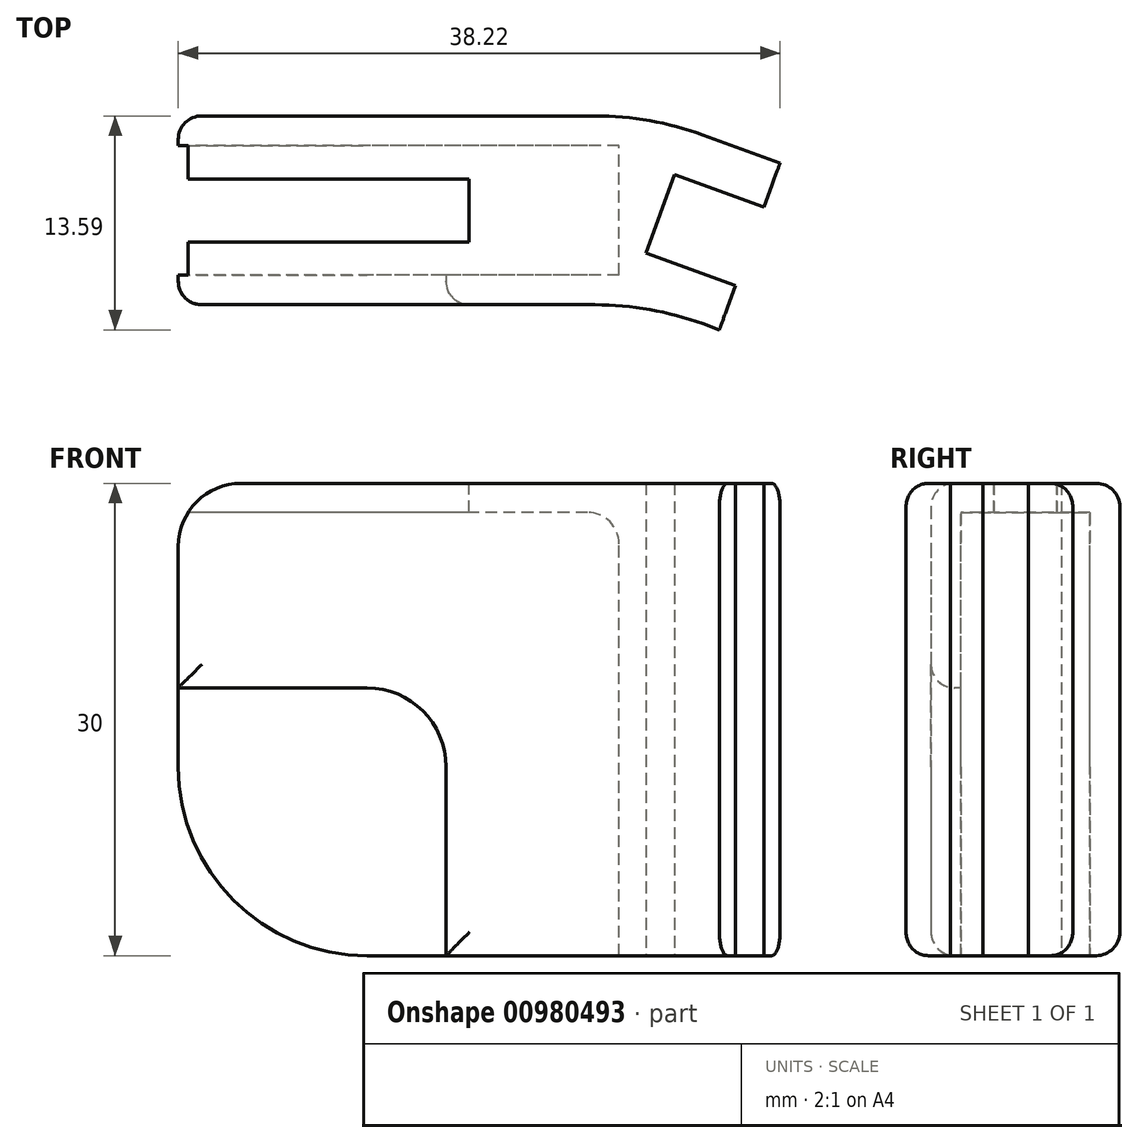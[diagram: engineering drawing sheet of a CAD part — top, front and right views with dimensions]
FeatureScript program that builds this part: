
annotation { "Feature Type Name" : "Feature", "Feature Type Description" : "" }
export const myFeature = defineFeature(function(context is Context, id is Id, definition is map)
    precondition{}
    {
        {
            var Q0;
            Q0=qCreatedBy(makeId("Top.planeOp"),FACE);
            var sketch = newSketch(context, id + "F0", { "sketchPlane" : qUnion([Q0])});
            skLineSegment(sketch, "E0.bottom", {"start": v(0, 0) * mm, "end": v(-30, 0) * mm});
            skLineSegment(sketch, "E0.top", {"start": v(0, 12) * mm, "end": v(-30, 12) * mm});
            skLineSegment(sketch, "E0.left", {"start": v(0, 0) * mm, "end": v(0, 12) * mm});
            skLineSegment(sketch, "E0.right", {"start": v(-30, 0) * mm, "end": v(-30, 12) * mm});
            skLineSegment(sketch, "E1", {"start": v(0, 12) * mm, "end": v(7.52, 9.26) * mm});
            skLineSegment(sketch, "E2", {"start": v(7.52, 9.26) * mm, "end": v(3.66, -1.33) * mm});
            skLineSegment(sketch, "E3", {"start": v(3.66, -1.33) * mm, "end": v(0, 0) * mm});
            skSolve(sketch);
        }
        {
            var Q0;
            Q0=makeQuery(id+"F0.imprint","IMPRINT",FACE,{"disambiguationData":[TD([[makeQuery(id+"F0.imprint","IMPRINT",EDGE,{"derivedFrom":sQuery(id+"F0.wireOp",EDGE,"E0.bottom")}),-1.0]])]});
            var Q1;
            Q1=makeQuery(id+"F0.imprint","IMPRINT",FACE,{"disambiguationData":[TD([[makeQuery(id+"F0.imprint","IMPRINT",EDGE,{"derivedFrom":sQuery(id+"F0.wireOp",EDGE,"E0.left")}),-1.0]])]});
            extrude(context, id + "F1", {"entities" : qUnion([Q0, Q1]), "depth" : 30 * mm, "offsetDistance" : 25 * mm});
        }
        {
            var Q0;
            Q0=makeQuery(id+"F1.opExtrude","SWEPT_FACE",FACE,{"disambiguationData":[OSD([sQuery(id+"F0.wireOp",EDGE,"E0.right")])]});
            var sketch = newSketch(context, id + "F2", { "sketchPlane" : qUnion([Q0])});
            skLineSegment(sketch, "E4.bottom", {"start": v(-10.1, 0) * mm, "end": v(-1.9, 0) * mm});
            skLineSegment(sketch, "E4.top", {"start": v(-10.1, 28.15) * mm, "end": v(-1.9, 28.15) * mm});
            skLineSegment(sketch, "E4.left", {"start": v(-10.1, 0) * mm, "end": v(-10.1, 28.15) * mm});
            skLineSegment(sketch, "E4.right", {"start": v(-1.9, 0) * mm, "end": v(-1.9, 28.15) * mm});
            skLineSegment(sketch, "E5", {"start": v(-10.1, 20.28) * mm, "end": v(-12, 20.28) * mm, "construction": true});
            skLineSegment(sketch, "E6", {"start": v(-1.9, 13.43) * mm, "end": v(0, 13.43) * mm, "construction": true});
            skSolve(sketch);
        }
        {
            var Q0;
            Q0=makeQuery(id+"F2.imprint","IMPRINT",FACE,{"disambiguationData":[TD([[makeQuery(id+"F2.imprint","IMPRINT",EDGE,{"derivedFrom":sQuery(id+"F2.wireOp",EDGE,"E4.bottom")}),-1.0]])]});
            extrude(context, id + "F3", {"entities" : qUnion([Q0]), "operationType" : NewBodyOperationType.REMOVE, "oppositeDirection" : true, "depth" : 28 * mm, "offsetDistance" : 25 * mm});
        }
        {
            var Q0;
            Q0=makeQuery(id+"F1.opExtrude","SWEPT_FACE",FACE,{"disambiguationData":[OSD([sQuery(id+"F0.wireOp",EDGE,"E2")])]});
            var sketch = newSketch(context, id + "F4", { "sketchPlane" : qUnion([Q0])});
            skLineSegment(sketch, "E7", {"start": v(2.99, 30) * mm, "end": v(2.99, 0) * mm});
            skLineSegment(sketch, "E8", {"start": v(8.29, 30) * mm, "end": v(8.29, 0) * mm});
            skLineSegment(sketch, "E9", {"start": v(0, 29.88) * mm, "end": v(2.99, 29.88) * mm, "construction": true});
            skLineSegment(sketch, "E10", {"start": v(8.29, 6.77) * mm, "end": v(11.28, 6.77) * mm, "construction": true});
            skSolve(sketch);
        }
        {
            var Q0;
            {var subQ0=sQuery(id+"F4.wireOp",EDGE,"E7");Q0=makeQuery(id+"F4.imprint","IMPRINT",FACE,{"disambiguationData":[TD([[makeQuery(id+"F4.imprint","IMPRINT",EDGE,{"derivedFrom":subQ0}),1.0]])]});}
            extrude(context, id + "F5", {"entities" : qUnion([Q0]), "operationType" : NewBodyOperationType.REMOVE, "oppositeDirection" : true, "depth" : 5.3 * mm, "offsetDistance" : 25 * mm});
        }
        {
            var Q0;
            Q0=makeQuery(id+"F1.opExtrude","SWEPT_FACE",FACE,{"disambiguationData":[OSD([sQuery(id+"F0.wireOp",EDGE,"E0.bottom")])]});
            var sketch = newSketch(context, id + "F6", { "sketchPlane" : qUnion([Q0])});
            skLineSegment(sketch, "E11.bottom", {"start": v(-30, 17) * mm, "end": v(-13, 17) * mm});
            skLineSegment(sketch, "E11.top", {"start": v(-30, 0) * mm, "end": v(-13, 0) * mm});
            skLineSegment(sketch, "E11.left", {"start": v(-30, 17) * mm, "end": v(-30, 0) * mm});
            skLineSegment(sketch, "E11.right", {"start": v(-13, 17) * mm, "end": v(-13, 0) * mm});
            skSolve(sketch);
        }
        {
            var Q0;
            Q0=makeQuery(id+"F6.imprint","IMPRINT",FACE,{"disambiguationData":[TD([[makeQuery(id+"F6.imprint","IMPRINT",EDGE,{"derivedFrom":sQuery(id+"F6.wireOp",EDGE,"E11.bottom")}),-1.0]])]});
            extrude(context, id + "F7", {"entities" : qUnion([Q0]), "operationType" : NewBodyOperationType.REMOVE, "oppositeDirection" : true, "depth" : 2.8 * mm, "offsetDistance" : 25 * mm});
        }
        {
            var Q0;
            {var subQ1=sQuery(id+"F0.wireOp",EDGE,"E2");var subQ2=sQuery(id+"F0.wireOp",EDGE,"E1");Q0=makeQuery(id+"F5.boolean.opBoolean","SPLIT",FACE,{"disambiguationData":[TD([makeQuery(id+"F1.opExtrude","SWEPT_FACE",FACE,{"disambiguationData":[OSD([subQ2])]})])],"derivedFrom":makeQuery(id+"F1.opExtrude","SWEPT_FACE",FACE,{"disambiguationData":[OSD([subQ1])]})});}
            var Q1;
            {var subQ0=sQuery(id+"F0.wireOp",EDGE,"E3");var subQ1=sQuery(id+"F0.wireOp",EDGE,"E2");Q1=makeQuery(id+"F5.boolean.opBoolean","SPLIT",FACE,{"disambiguationData":[TD([makeQuery(id+"F1.opExtrude","SWEPT_FACE",FACE,{"disambiguationData":[OSD([subQ0])]})])],"derivedFrom":makeQuery(id+"F1.opExtrude","SWEPT_FACE",FACE,{"disambiguationData":[OSD([subQ1])]})});}
            extrude(context, id + "F8", {"entities" : qUnion([Q0, Q1]), "operationType" : NewBodyOperationType.ADD, "depth" : .75 * mm, "offsetDistance" : 25 * mm});
        }
        {
            var Q0;
            {var subQ0=sQuery(id+"F0.wireOp",EDGE,"E0.right");var subQ1=sQuery(id+"F0.wireOp",EDGE,"E0.top");Q0=makeQuery(id+"F3.boolean.opBoolean","SPLIT",EDGE,{"disambiguationData":[TD([makeQuery(id+"F1.opExtrude","SWEPT_FACE",FACE,{"disambiguationData":[OSD([subQ1])]})])],"derivedFrom":makeQuery(id+"F1.opExtrude","CAP_EDGE",EDGE,{"disambiguationData":[OSD([subQ0])],"isStart":true})});}
            fillet(context, id + "F9", {"entities" : qUnion([Q0]), "radius" : 12 * mm, "tangentPropagation" : true, "allowEdgeOverflow" : false});
        }
        {
            var Q0;
            Q0=makeQuery(id+"F1.opExtrude","CAP_EDGE",EDGE,{"disambiguationData":[OSD([sQuery(id+"F0.wireOp",EDGE,"E0.right")])],"isStart":false});
            var Q1;
            Q1=makeQuery(id+"F7.boolean.opBoolean","COPY",EDGE,{"derivedFrom":makeQuery(id+"F7.opExtrude","SWEPT_EDGE",EDGE,{"disambiguationData":[OSD([sQuery(id+"F0.wireOp",EDGE,"E0.bottom"),sQuery(id+"F0.wireOp",EDGE,"E0.right"),sQuery(id+"F6.wireOp",EDGE,"E11.bottom"),sQuery(id+"F6.wireOp",EDGE,"E11.left")])]})});
            var Q2;
            Q2=makeQuery(id+"F7.boolean.opBoolean","COPY",EDGE,{"derivedFrom":makeQuery(id+"F7.opExtrude","SWEPT_EDGE",EDGE,{"disambiguationData":[OSD([sQuery(id+"F0.wireOp",EDGE,"E0.bottom"),sQuery(id+"F6.wireOp",EDGE,"E11.top"),sQuery(id+"F6.wireOp",EDGE,"E11.right")])]})});
            fillet(context, id + "F10", {"entities" : qUnion([Q0, Q1, Q2]), "radius" : 4 * mm, "tangentPropagation" : true, "allowEdgeOverflow" : false});
        }
        {
            var Q0;
            Q0=makeQuery(id+"F1.opExtrude","SWEPT_EDGE",EDGE,{"disambiguationData":[OSD([sQuery(id+"F0.wireOp",EDGE,"E0.top"),sQuery(id+"F0.wireOp",EDGE,"E0.left"),sQuery(id+"F0.wireOp",EDGE,"E1")])]});
            var Q1;
            Q1=makeQuery(id+"F1.opExtrude","SWEPT_EDGE",EDGE,{"disambiguationData":[OSD([sQuery(id+"F0.wireOp",EDGE,"E0.bottom"),sQuery(id+"F0.wireOp",EDGE,"E0.left"),sQuery(id+"F0.wireOp",EDGE,"E3")])]});
            fillet(context, id + "F11", {"entities" : qUnion([Q0, Q1]), "radius" : 20 * mm, "tangentPropagation" : true, "allowEdgeOverflow" : false});
        }
        {
            var Q0;
            Q0=makeQuery(id+"F7.boolean.opBoolean","COPY",EDGE,{"derivedFrom":makeQuery(id+"F7.opExtrude","SWEPT_EDGE",EDGE,{"disambiguationData":[OSD([sQuery(id+"F6.wireOp",EDGE,"E11.bottom"),sQuery(id+"F6.wireOp",EDGE,"E11.right")])]})});
            fillet(context, id + "F12", {"entities" : qUnion([Q0]), "radius" : 5 * mm, "tangentPropagation" : true, "allowEdgeOverflow" : false});
        }
        {
            var Q0;
            Q0=makeQuery(id+"F12.opFillet","BLEND_EDGE",EDGE,{"blendedFrom":[makeQuery(id+"F7.boolean.opBoolean","COPY",EDGE,{"derivedFrom":makeQuery(id+"F7.opExtrude","SWEPT_EDGE",EDGE,{"disambiguationData":[OSD([sQuery(id+"F6.wireOp",EDGE,"E11.bottom"),sQuery(id+"F6.wireOp",EDGE,"E11.right")])]})}),makeQuery(id+"F1.opExtrude","SWEPT_FACE",FACE,{"disambiguationData":[OSD([sQuery(id+"F0.wireOp",EDGE,"E0.bottom")])]})],"blendedInto":[makeQuery(id+"F1.opExtrude","SWEPT_FACE",FACE,{"disambiguationData":[OSD([sQuery(id+"F0.wireOp",EDGE,"E0.bottom")])]})]});
            var Q1;
            Q1=makeQuery(id+"F7.boolean.opBoolean","COPY",EDGE,{"derivedFrom":makeQuery(id+"F7.opExtrude","CAP_EDGE",EDGE,{"disambiguationData":[OSD([sQuery(id+"F6.wireOp",EDGE,"E11.bottom")])],"isStart":true})});
            var Q2;
            Q2=makeQuery(id+"F10.opFillet","BLEND_EDGE",EDGE,{"blendedFrom":[makeQuery(id+"F1.opExtrude","CAP_EDGE",EDGE,{"disambiguationData":[OSD([sQuery(id+"F0.wireOp",EDGE,"E0.right")])],"isStart":false}),makeQuery(id+"F1.opExtrude","SWEPT_FACE",FACE,{"disambiguationData":[OSD([sQuery(id+"F0.wireOp",EDGE,"E0.bottom")])]})],"blendedInto":[makeQuery(id+"F1.opExtrude","SWEPT_FACE",FACE,{"disambiguationData":[OSD([sQuery(id+"F0.wireOp",EDGE,"E0.bottom")])]})]});
            var Q3;
            Q3=makeQuery(id+"F1.opExtrude","CAP_EDGE",EDGE,{"disambiguationData":[OSD([sQuery(id+"F0.wireOp",EDGE,"E0.bottom")])],"isStart":false});
            var Q4;
            {var subQ0=sQuery(id+"F0.wireOp",EDGE,"E3");var subQ1=sQuery(id+"F0.wireOp",EDGE,"E0.bottom");Q4=makeQuery(id+"F11.opFillet","BLEND_EDGE",EDGE,{"blendedFrom":[makeQuery(id+"F1.opExtrude","SWEPT_EDGE",EDGE,{"disambiguationData":[OSD([subQ1,sQuery(id+"F0.wireOp",EDGE,"E0.left"),subQ0])]}),makeQuery(id+"F1.opExtrude","CAP_FACE",FACE,{"disambiguationData":[OSD([subQ1,sQuery(id+"F0.wireOp",EDGE,"E0.top"),sQuery(id+"F0.wireOp",EDGE,"E0.right"),sQuery(id+"F0.wireOp",EDGE,"E1"),sQuery(id+"F0.wireOp",EDGE,"E2"),subQ0])],"isStart":false})],"blendedInto":[makeQuery(id+"F1.opExtrude","CAP_FACE",FACE,{"disambiguationData":[OSD([subQ1,sQuery(id+"F0.wireOp",EDGE,"E0.top"),sQuery(id+"F0.wireOp",EDGE,"E0.right"),sQuery(id+"F0.wireOp",EDGE,"E1"),sQuery(id+"F0.wireOp",EDGE,"E2"),subQ0])],"isStart":false})]});}
            var Q5;
            Q5=makeQuery(id+"F1.opExtrude","CAP_EDGE",EDGE,{"disambiguationData":[OSD([sQuery(id+"F0.wireOp",EDGE,"E3")])],"isStart":false});
            var Q6;
            Q6=makeQuery(id+"F1.opExtrude","SWEPT_EDGE",EDGE,{"disambiguationData":[OSD([sQuery(id+"F0.wireOp",EDGE,"E2"),sQuery(id+"F0.wireOp",EDGE,"E3")])]});
            var Q7;
            Q7=makeQuery(id+"F1.opExtrude","CAP_EDGE",EDGE,{"disambiguationData":[OSD([sQuery(id+"F0.wireOp",EDGE,"E3")])],"isStart":true});
            var Q8;
            {var subQ0=sQuery(id+"F0.wireOp",EDGE,"E3");var subQ1=sQuery(id+"F0.wireOp",EDGE,"E0.bottom");Q8=makeQuery(id+"F11.opFillet","BLEND_EDGE",EDGE,{"blendedFrom":[makeQuery(id+"F1.opExtrude","SWEPT_EDGE",EDGE,{"disambiguationData":[OSD([subQ1,sQuery(id+"F0.wireOp",EDGE,"E0.left"),subQ0])]}),makeQuery(id+"F1.opExtrude","CAP_FACE",FACE,{"disambiguationData":[OSD([subQ1,sQuery(id+"F0.wireOp",EDGE,"E0.top"),sQuery(id+"F0.wireOp",EDGE,"E0.right"),sQuery(id+"F0.wireOp",EDGE,"E1"),sQuery(id+"F0.wireOp",EDGE,"E2"),subQ0])],"isStart":true})],"blendedInto":[makeQuery(id+"F1.opExtrude","CAP_FACE",FACE,{"disambiguationData":[OSD([subQ1,sQuery(id+"F0.wireOp",EDGE,"E0.top"),sQuery(id+"F0.wireOp",EDGE,"E0.right"),sQuery(id+"F0.wireOp",EDGE,"E1"),sQuery(id+"F0.wireOp",EDGE,"E2"),subQ0])],"isStart":true})]});}
            var Q9;
            Q9=makeQuery(id+"F1.opExtrude","CAP_EDGE",EDGE,{"disambiguationData":[OSD([sQuery(id+"F0.wireOp",EDGE,"E0.bottom")])],"isStart":true});
            var Q10;
            {var subQ0=sQuery(id+"F0.wireOp",EDGE,"E0.bottom");Q10=makeQuery(id+"F10.opFillet","BLEND_EDGE",EDGE,{"blendedFrom":[makeQuery(id+"F7.boolean.opBoolean","COPY",EDGE,{"derivedFrom":makeQuery(id+"F7.opExtrude","SWEPT_EDGE",EDGE,{"disambiguationData":[OSD([subQ0,sQuery(id+"F6.wireOp",EDGE,"E11.top"),sQuery(id+"F6.wireOp",EDGE,"E11.right")])]})}),makeQuery(id+"F1.opExtrude","SWEPT_FACE",FACE,{"disambiguationData":[OSD([subQ0])]})],"blendedInto":[makeQuery(id+"F1.opExtrude","SWEPT_FACE",FACE,{"disambiguationData":[OSD([subQ0])]})]});}
            var Q11;
            Q11=makeQuery(id+"F7.boolean.opBoolean","COPY",EDGE,{"derivedFrom":makeQuery(id+"F7.opExtrude","CAP_EDGE",EDGE,{"disambiguationData":[OSD([sQuery(id+"F6.wireOp",EDGE,"E11.right")])],"isStart":true})});
            var Q12;
            Q12=makeQuery(id+"F1.opExtrude","CAP_EDGE",EDGE,{"disambiguationData":[OSD([sQuery(id+"F0.wireOp",EDGE,"E0.top")])],"isStart":false});
            var Q13;
            {var subQ0=sQuery(id+"F0.wireOp",EDGE,"E1");var subQ1=sQuery(id+"F0.wireOp",EDGE,"E0.top");Q13=makeQuery(id+"F11.opFillet","BLEND_EDGE",EDGE,{"blendedFrom":[makeQuery(id+"F1.opExtrude","SWEPT_EDGE",EDGE,{"disambiguationData":[OSD([subQ1,sQuery(id+"F0.wireOp",EDGE,"E0.left"),subQ0])]}),makeQuery(id+"F1.opExtrude","CAP_FACE",FACE,{"disambiguationData":[OSD([sQuery(id+"F0.wireOp",EDGE,"E0.bottom"),subQ1,sQuery(id+"F0.wireOp",EDGE,"E0.right"),subQ0,sQuery(id+"F0.wireOp",EDGE,"E2"),sQuery(id+"F0.wireOp",EDGE,"E3")])],"isStart":false})],"blendedInto":[makeQuery(id+"F1.opExtrude","CAP_FACE",FACE,{"disambiguationData":[OSD([sQuery(id+"F0.wireOp",EDGE,"E0.bottom"),subQ1,sQuery(id+"F0.wireOp",EDGE,"E0.right"),subQ0,sQuery(id+"F0.wireOp",EDGE,"E2"),sQuery(id+"F0.wireOp",EDGE,"E3")])],"isStart":false})]});}
            var Q14;
            Q14=makeQuery(id+"F1.opExtrude","SWEPT_EDGE",EDGE,{"disambiguationData":[OSD([sQuery(id+"F0.wireOp",EDGE,"E1"),sQuery(id+"F0.wireOp",EDGE,"E2")])]});
            fillet(context, id + "F13", {"entities" : qUnion([Q0, Q1, Q2, Q3, Q4, Q5, Q6, Q7, Q8, Q9, Q10, Q11, Q12, Q13, Q14]), "radius" : 1.5 * mm, "tangentPropagation" : true, "allowEdgeOverflow" : false});
        }
        {
            var Q0;
            Q0=makeQuery(id+"F3.boolean.opBoolean","COPY",EDGE,{"derivedFrom":makeQuery(id+"F3.opExtrude","CAP_EDGE",EDGE,{"disambiguationData":[OSD([sQuery(id+"F2.wireOp",EDGE,"E4.top")])],"isStart":false})});
            fillet(context, id + "F14", {"entities" : qUnion([Q0]), "radius" : 2 * mm, "tangentPropagation" : true, "allowEdgeOverflow" : false});
        }
        {
            var Q0;
            {var subQ0=sQuery(id+"F0.wireOp",EDGE,"E3");var subQ1=sQuery(id+"F0.wireOp",EDGE,"E2");var subQ2=sQuery(id+"F0.wireOp",EDGE,"E1");var subQ3=makeQuery(id+"F1.opExtrude","CAP_FACE",FACE,{"disambiguationData":[OSD([sQuery(id+"F0.wireOp",EDGE,"E0.bottom"),sQuery(id+"F0.wireOp",EDGE,"E0.top"),sQuery(id+"F0.wireOp",EDGE,"E0.right"),subQ2,subQ1,subQ0])],"isStart":false});var subQ5=makeQuery(id+"F1.opExtrude","CAP_EDGE",EDGE,{"disambiguationData":[OSD([subQ1])],"isStart":false});Q0=makeQuery(id+"F8.boolean.opBoolean","MERGE",FACE,{"derivedFrom":[subQ3,makeQuery(id+"F8.opExtrude","SWEPT_FACE",FACE,{"disambiguationData":[OSD([subQ1]),TDD([makeQuery(id+"F5.boolean.opBoolean","SPLIT",EDGE,{"disambiguationData":[TD([makeQuery(id+"F1.opExtrude","SWEPT_FACE",FACE,{"disambiguationData":[OSD([subQ2])]})])],"derivedFrom":subQ5})])]}),makeQuery(id+"F8.opExtrude","SWEPT_FACE",FACE,{"disambiguationData":[OSD([subQ1]),TDD([makeQuery(id+"F5.boolean.opBoolean","SPLIT",EDGE,{"disambiguationData":[TD([makeQuery(id+"F1.opExtrude","SWEPT_FACE",FACE,{"disambiguationData":[OSD([subQ0])]})])],"derivedFrom":subQ5})])]})]});}
            var sketch = newSketch(context, id + "F15", { "sketchPlane" : qUnion([Q0])});
            skLineSegment(sketch, "E12", {"start": v(-31.09, 6) * mm, "end": v(6.32, 6) * mm, "construction": true});
            skPoint(sketch, "E12.startSnap0", {"position": v(-26, 6) * mm});
            skLineSegment(sketch, "E13.bottom", {"start": v(-31.09, 8) * mm, "end": v(-11.53, 8) * mm});
            skLineSegment(sketch, "E13.top", {"start": v(-31.09, 4) * mm, "end": v(-11.53, 4) * mm});
            skLineSegment(sketch, "E13.left", {"start": v(-31.09, 8) * mm, "end": v(-31.09, 4) * mm});
            skLineSegment(sketch, "E13.right", {"start": v(-11.53, 8) * mm, "end": v(-11.53, 4) * mm});
            skSolve(sketch);
        }
        {
            var Q0;
            {var subQ0=sQuery(id+"F15.wireOp",EDGE,"E13.left");Q0=makeQuery(id+"F15.imprint","IMPRINT",FACE,{"disambiguationData":[TD([[makeQuery(id+"F15.imprint","IMPRINT",EDGE,{"derivedFrom":subQ0}),1.0]])]});}
            var Q1;
            {var subQ0=sQuery(id+"F15.wireOp",EDGE,"E13.right");Q1=makeQuery(id+"F15.imprint","IMPRINT",FACE,{"disambiguationData":[TD([[makeQuery(id+"F15.imprint","IMPRINT",EDGE,{"derivedFrom":subQ0}),-1.0]])]});}
            extrude(context, id + "F16", {"entities" : qUnion([Q0, Q1]), "operationType" : NewBodyOperationType.REMOVE, "endBound" : BoundingType.THROUGH_ALL, "oppositeDirection" : true, "depth" : 25 * mm, "offsetDistance" : 25 * mm});
        }
    });
